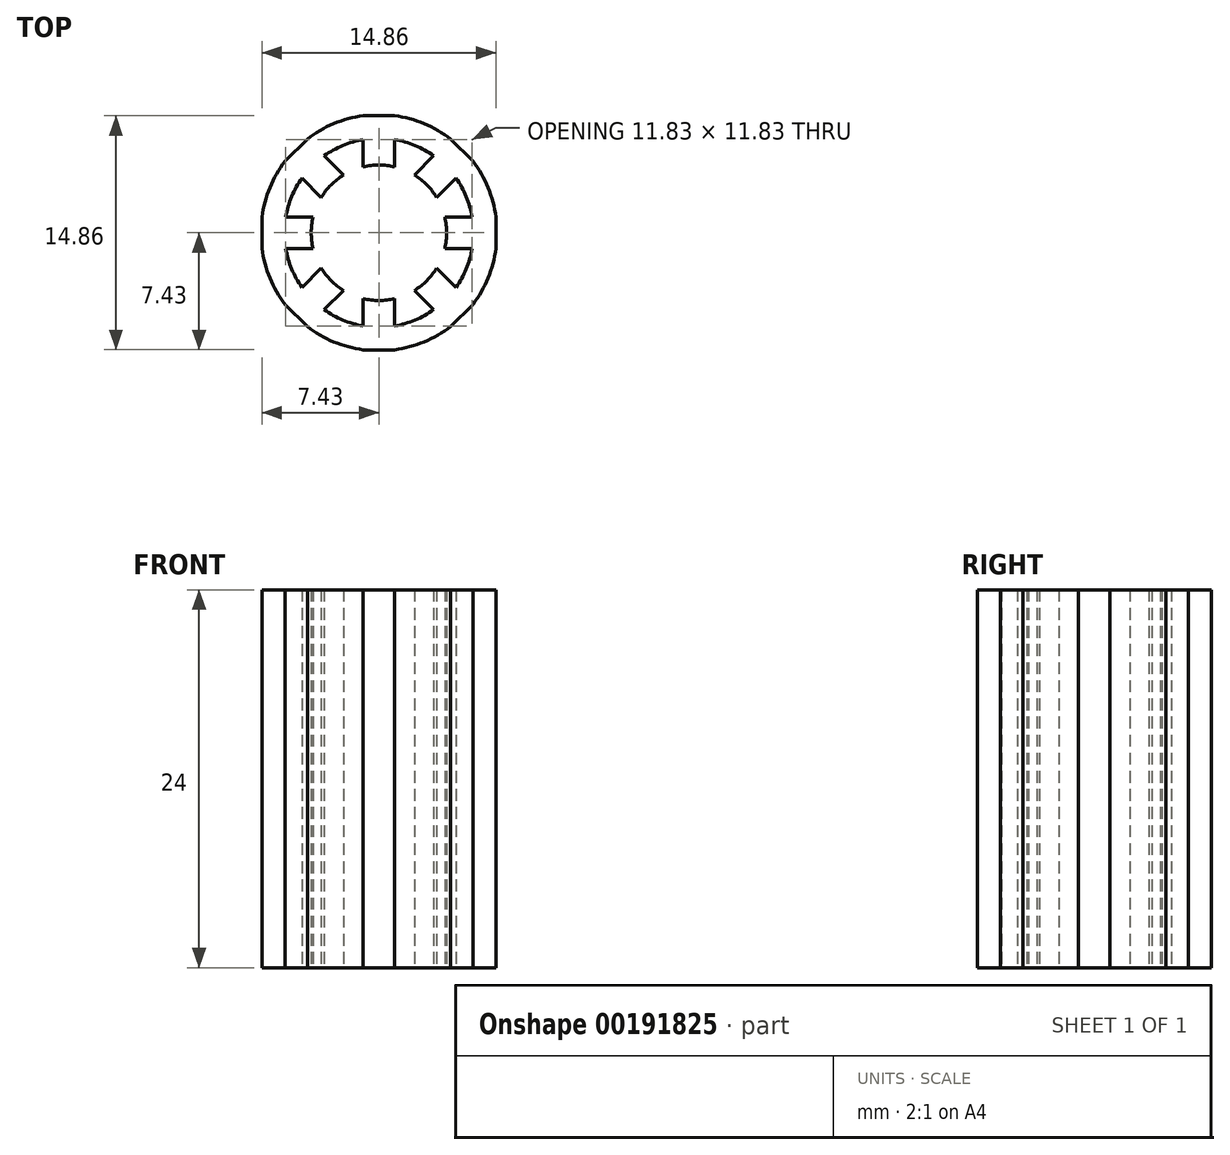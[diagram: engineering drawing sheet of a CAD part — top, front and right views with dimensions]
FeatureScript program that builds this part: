
annotation { "Feature Type Name" : "Feature", "Feature Type Description" : "" }
export const myFeature = defineFeature(function(context is Context, id is Id, definition is map)
    precondition{}
    {
        {
            var Q0;
            Q0=qCreatedBy(makeId("Top.planeOp"),FACE);
            var sketch = newSketch(context, id + "F0", { "sketchPlane" : qUnion([Q0])});
            skCircle(sketch, "E0", {"center": v(0, 0) * mm, "radius": 7.5 * mm});
            skCircle(sketch, "E1", {"center": v(0, 0) * mm, "radius": 4.3 * mm});
            skCircle(sketch, "E2", {"center": v(0, 0) * mm, "radius": 6 * mm});
            skLineSegment(sketch, "E3.bottom", {"start": v(7.43, -1) * mm, "end": v(-7.43, -1) * mm});
            skLineSegment(sketch, "E3.top", {"start": v(7.43, 1) * mm, "end": v(-7.43, 1) * mm});
            skLineSegment(sketch, "E3.left", {"start": v(7.43, -1) * mm, "end": v(7.43, 1) * mm});
            skLineSegment(sketch, "E3.right", {"start": v(-7.43, -1) * mm, "end": v(-7.43, 1) * mm});
            skLineSegment(sketch, "E4.bottom", {"start": v(1, 7.43) * mm, "end": v(-1, 7.43) * mm});
            skLineSegment(sketch, "E4.top", {"start": v(1, -7.43) * mm, "end": v(-1, -7.43) * mm});
            skLineSegment(sketch, "E4.left", {"start": v(1, 7.43) * mm, "end": v(1, -7.43) * mm});
            skLineSegment(sketch, "E4.right", {"start": v(-1, 7.43) * mm, "end": v(-1, -7.43) * mm});
            skLineSegment(sketch, "E5.bottom", {"start": v(-5.96, 4.55) * mm, "end": v(-4.55, 5.96) * mm});
            skLineSegment(sketch, "E5.top", {"start": v(4.55, -5.96) * mm, "end": v(5.96, -4.55) * mm});
            skLineSegment(sketch, "E5.left", {"start": v(-5.96, 4.55) * mm, "end": v(4.55, -5.96) * mm});
            skLineSegment(sketch, "E5.right", {"start": v(-4.55, 5.96) * mm, "end": v(5.96, -4.55) * mm});
            skLineSegment(sketch, "E6.bottom", {"start": v(5.96, 4.55) * mm, "end": v(4.55, 5.96) * mm});
            skLineSegment(sketch, "E6.top", {"start": v(-4.55, -5.96) * mm, "end": v(-5.96, -4.55) * mm});
            skLineSegment(sketch, "E6.left", {"start": v(5.96, 4.55) * mm, "end": v(-4.55, -5.96) * mm});
            skLineSegment(sketch, "E6.right", {"start": v(4.55, 5.96) * mm, "end": v(-5.96, -4.55) * mm});
            skSolve(sketch);
        }
        {
            var Q0;
            {var subQ5=sQuery(id+"F0.wireOp",EDGE,"E3.right");Q0=makeQuery(id+"F0.imprint","IMPRINT",FACE,{"disambiguationData":[TD([[makeQuery(id+"F0.imprint","IMPRINT",EDGE,{"derivedFrom":subQ5}),-1.0]])]});}
            var Q1;
            {var subQ0=sQuery(id+"F0.wireOp",EDGE,"E3.bottom");var subQ5=sQuery(id+"F0.wireOp",EDGE,"E2");var subQ6=makeQuery(id+"F0.imprint","INTERSECT",VERTEX,{"disambiguationData":[OD(0.0)],"derivedFrom":[subQ5,subQ0]});Q1=makeQuery(id+"F0.imprint","IMPRINT",FACE,{"disambiguationData":[TD([[makeQuery(id+"F0.imprint","IMPRINT",EDGE,{"disambiguationData":[TD([[subQ6,-1.0]])],"derivedFrom":subQ5}),-1.0]])]});}
            var Q2;
            {var subQ5=sQuery(id+"F0.wireOp",EDGE,"E6.top");Q2=makeQuery(id+"F0.imprint","IMPRINT",FACE,{"disambiguationData":[TD([[makeQuery(id+"F0.imprint","IMPRINT",EDGE,{"derivedFrom":subQ5}),-1.0]])]});}
            var Q3;
            {var subQ3=sQuery(id+"F0.wireOp",EDGE,"E6.left");var subQ5=sQuery(id+"F0.wireOp",EDGE,"E2");var subQ7=makeQuery(id+"F0.imprint","INTERSECT",VERTEX,{"disambiguationData":[OD(1.0)],"derivedFrom":[subQ5,subQ3]});Q3=makeQuery(id+"F0.imprint","IMPRINT",FACE,{"disambiguationData":[TD([[makeQuery(id+"F0.imprint","IMPRINT",EDGE,{"disambiguationData":[TD([[subQ7,-1.0]])],"derivedFrom":subQ5}),-1.0]])]});}
            var Q4;
            {var subQ5=sQuery(id+"F0.wireOp",EDGE,"E4.top");Q4=makeQuery(id+"F0.imprint","IMPRINT",FACE,{"disambiguationData":[TD([[makeQuery(id+"F0.imprint","IMPRINT",EDGE,{"derivedFrom":subQ5}),-1.0]])]});}
            var Q5;
            {var subQ0=sQuery(id+"F0.wireOp",EDGE,"E4.left");var subQ5=sQuery(id+"F0.wireOp",EDGE,"E2");var subQ6=makeQuery(id+"F0.imprint","INTERSECT",VERTEX,{"disambiguationData":[OD(1.0)],"derivedFrom":[subQ5,subQ0]});Q5=makeQuery(id+"F0.imprint","IMPRINT",FACE,{"disambiguationData":[TD([[makeQuery(id+"F0.imprint","IMPRINT",EDGE,{"disambiguationData":[TD([[subQ6,-1.0]])],"derivedFrom":subQ5}),-1.0]])]});}
            var Q6;
            {var subQ5=sQuery(id+"F0.wireOp",EDGE,"E5.top");Q6=makeQuery(id+"F0.imprint","IMPRINT",FACE,{"disambiguationData":[TD([[makeQuery(id+"F0.imprint","IMPRINT",EDGE,{"derivedFrom":subQ5}),1.0]])]});}
            var Q7;
            {var subQ3=sQuery(id+"F0.wireOp",EDGE,"E5.right");var subQ5=sQuery(id+"F0.wireOp",EDGE,"E2");var subQ6=makeQuery(id+"F0.imprint","INTERSECT",VERTEX,{"disambiguationData":[OD(1.0)],"derivedFrom":[subQ5,subQ3]});Q7=makeQuery(id+"F0.imprint","IMPRINT",FACE,{"disambiguationData":[TD([[makeQuery(id+"F0.imprint","IMPRINT",EDGE,{"disambiguationData":[TD([[subQ6,-1.0]])],"derivedFrom":subQ5}),-1.0]])]});}
            var Q8;
            {var subQ5=sQuery(id+"F0.wireOp",EDGE,"E3.left");Q8=makeQuery(id+"F0.imprint","IMPRINT",FACE,{"disambiguationData":[TD([[makeQuery(id+"F0.imprint","IMPRINT",EDGE,{"derivedFrom":subQ5}),1.0]])]});}
            var Q9;
            {var subQ3=sQuery(id+"F0.wireOp",EDGE,"E6.left");var subQ5=sQuery(id+"F0.wireOp",EDGE,"E2");var subQ6=makeQuery(id+"F0.imprint","INTERSECT",VERTEX,{"disambiguationData":[OD(0.0)],"derivedFrom":[subQ5,subQ3]});Q9=makeQuery(id+"F0.imprint","IMPRINT",FACE,{"disambiguationData":[TD([[makeQuery(id+"F0.imprint","IMPRINT",EDGE,{"disambiguationData":[TD([[subQ6,1.0]])],"derivedFrom":subQ5}),-1.0]])]});}
            var Q10;
            {var subQ5=sQuery(id+"F0.wireOp",EDGE,"E6.bottom");Q10=makeQuery(id+"F0.imprint","IMPRINT",FACE,{"disambiguationData":[TD([[makeQuery(id+"F0.imprint","IMPRINT",EDGE,{"derivedFrom":subQ5}),1.0]])]});}
            var Q11;
            {var subQ3=sQuery(id+"F0.wireOp",EDGE,"E6.right");var subQ5=sQuery(id+"F0.wireOp",EDGE,"E2");var subQ6=makeQuery(id+"F0.imprint","INTERSECT",VERTEX,{"disambiguationData":[OD(0.0)],"derivedFrom":[subQ5,subQ3]});Q11=makeQuery(id+"F0.imprint","IMPRINT",FACE,{"disambiguationData":[TD([[makeQuery(id+"F0.imprint","IMPRINT",EDGE,{"disambiguationData":[TD([[subQ6,-1.0]])],"derivedFrom":subQ5}),-1.0]])]});}
            var Q12;
            {var subQ5=sQuery(id+"F0.wireOp",EDGE,"E4.bottom");Q12=makeQuery(id+"F0.imprint","IMPRINT",FACE,{"disambiguationData":[TD([[makeQuery(id+"F0.imprint","IMPRINT",EDGE,{"derivedFrom":subQ5}),1.0]])]});}
            var Q13;
            {var subQ0=sQuery(id+"F0.wireOp",EDGE,"E4.right");var subQ5=sQuery(id+"F0.wireOp",EDGE,"E2");var subQ6=makeQuery(id+"F0.imprint","INTERSECT",VERTEX,{"disambiguationData":[OD(0.0)],"derivedFrom":[subQ5,subQ0]});Q13=makeQuery(id+"F0.imprint","IMPRINT",FACE,{"disambiguationData":[TD([[makeQuery(id+"F0.imprint","IMPRINT",EDGE,{"disambiguationData":[TD([[subQ6,-1.0]])],"derivedFrom":subQ5}),-1.0]])]});}
            var Q14;
            {var subQ5=sQuery(id+"F0.wireOp",EDGE,"E5.bottom");Q14=makeQuery(id+"F0.imprint","IMPRINT",FACE,{"disambiguationData":[TD([[makeQuery(id+"F0.imprint","IMPRINT",EDGE,{"derivedFrom":subQ5}),-1.0]])]});}
            var Q15;
            {var subQ3=sQuery(id+"F0.wireOp",EDGE,"E5.left");var subQ5=sQuery(id+"F0.wireOp",EDGE,"E2");var subQ6=makeQuery(id+"F0.imprint","INTERSECT",VERTEX,{"disambiguationData":[OD(0.0)],"derivedFrom":[subQ5,subQ3]});Q15=makeQuery(id+"F0.imprint","IMPRINT",FACE,{"disambiguationData":[TD([[makeQuery(id+"F0.imprint","IMPRINT",EDGE,{"disambiguationData":[TD([[subQ6,-1.0]])],"derivedFrom":subQ5}),-1.0]])]});}
            var Q16;
            {var subQ0=sQuery(id+"F0.wireOp",EDGE,"E5.right");var subQ1=sQuery(id+"F0.wireOp",EDGE,"E1");var subQ2=makeQuery(id+"F0.imprint","INTERSECT",VERTEX,{"disambiguationData":[OD(0.0)],"derivedFrom":[subQ1,subQ0]});Q16=makeQuery(id+"F0.imprint","IMPRINT",FACE,{"disambiguationData":[TD([[makeQuery(id+"F0.imprint","IMPRINT",EDGE,{"disambiguationData":[TD([[subQ2,-1.0]])],"derivedFrom":subQ1}),-1.0]])]});}
            var Q17;
            {var subQ0=sQuery(id+"F0.wireOp",EDGE,"E4.left");var subQ1=sQuery(id+"F0.wireOp",EDGE,"E1");var subQ2=makeQuery(id+"F0.imprint","INTERSECT",VERTEX,{"disambiguationData":[OD(0.0)],"derivedFrom":[subQ1,subQ0]});Q17=makeQuery(id+"F0.imprint","IMPRINT",FACE,{"disambiguationData":[TD([[makeQuery(id+"F0.imprint","IMPRINT",EDGE,{"disambiguationData":[TD([[subQ2,-1.0]])],"derivedFrom":subQ1}),-1.0]])]});}
            var Q18;
            {var subQ0=sQuery(id+"F0.wireOp",EDGE,"E6.left");var subQ1=sQuery(id+"F0.wireOp",EDGE,"E1");var subQ2=makeQuery(id+"F0.imprint","INTERSECT",VERTEX,{"disambiguationData":[OD(0.0)],"derivedFrom":[subQ1,subQ0]});Q18=makeQuery(id+"F0.imprint","IMPRINT",FACE,{"disambiguationData":[TD([[makeQuery(id+"F0.imprint","IMPRINT",EDGE,{"disambiguationData":[TD([[subQ2,-1.0]])],"derivedFrom":subQ1}),-1.0]])]});}
            var Q19;
            {var subQ0=sQuery(id+"F0.wireOp",EDGE,"E3.top");var subQ1=sQuery(id+"F0.wireOp",EDGE,"E1");var subQ2=makeQuery(id+"F0.imprint","INTERSECT",VERTEX,{"disambiguationData":[OD(0.0)],"derivedFrom":[subQ1,subQ0]});Q19=makeQuery(id+"F0.imprint","IMPRINT",FACE,{"disambiguationData":[TD([[makeQuery(id+"F0.imprint","IMPRINT",EDGE,{"disambiguationData":[TD([[subQ2,1.0]])],"derivedFrom":subQ1}),-1.0]])]});}
            var Q20;
            {var subQ0=sQuery(id+"F0.wireOp",EDGE,"E5.left");var subQ1=sQuery(id+"F0.wireOp",EDGE,"E1");var subQ2=makeQuery(id+"F0.imprint","INTERSECT",VERTEX,{"disambiguationData":[OD(1.0)],"derivedFrom":[subQ1,subQ0]});Q20=makeQuery(id+"F0.imprint","IMPRINT",FACE,{"disambiguationData":[TD([[makeQuery(id+"F0.imprint","IMPRINT",EDGE,{"disambiguationData":[TD([[subQ2,-1.0]])],"derivedFrom":subQ1}),-1.0]])]});}
            var Q21;
            {var subQ0=sQuery(id+"F0.wireOp",EDGE,"E4.right");var subQ1=sQuery(id+"F0.wireOp",EDGE,"E1");var subQ2=makeQuery(id+"F0.imprint","INTERSECT",VERTEX,{"disambiguationData":[OD(1.0)],"derivedFrom":[subQ1,subQ0]});Q21=makeQuery(id+"F0.imprint","IMPRINT",FACE,{"disambiguationData":[TD([[makeQuery(id+"F0.imprint","IMPRINT",EDGE,{"disambiguationData":[TD([[subQ2,-1.0]])],"derivedFrom":subQ1}),-1.0]])]});}
            var Q22;
            {var subQ0=sQuery(id+"F0.wireOp",EDGE,"E6.right");var subQ1=sQuery(id+"F0.wireOp",EDGE,"E1");var subQ2=makeQuery(id+"F0.imprint","INTERSECT",VERTEX,{"disambiguationData":[OD(1.0)],"derivedFrom":[subQ1,subQ0]});Q22=makeQuery(id+"F0.imprint","IMPRINT",FACE,{"disambiguationData":[TD([[makeQuery(id+"F0.imprint","IMPRINT",EDGE,{"disambiguationData":[TD([[subQ2,-1.0]])],"derivedFrom":subQ1}),-1.0]])]});}
            var Q23;
            {var subQ0=sQuery(id+"F0.wireOp",EDGE,"E3.top");var subQ1=sQuery(id+"F0.wireOp",EDGE,"E1");var subQ2=makeQuery(id+"F0.imprint","INTERSECT",VERTEX,{"disambiguationData":[OD(1.0)],"derivedFrom":[subQ1,subQ0]});Q23=makeQuery(id+"F0.imprint","IMPRINT",FACE,{"disambiguationData":[TD([[makeQuery(id+"F0.imprint","IMPRINT",EDGE,{"disambiguationData":[TD([[subQ2,-1.0]])],"derivedFrom":subQ1}),-1.0]])]});}
            extrude(context, id + "F1", {"entities" : qUnion([Q0, Q1, Q2, Q3, Q4, Q5, Q6, Q7, Q8, Q9, Q10, Q11, Q12, Q13, Q14, Q15, Q16, Q17, Q18, Q19, Q20, Q21, Q22, Q23]), "depth" : 24 * mm});
        }
    });
